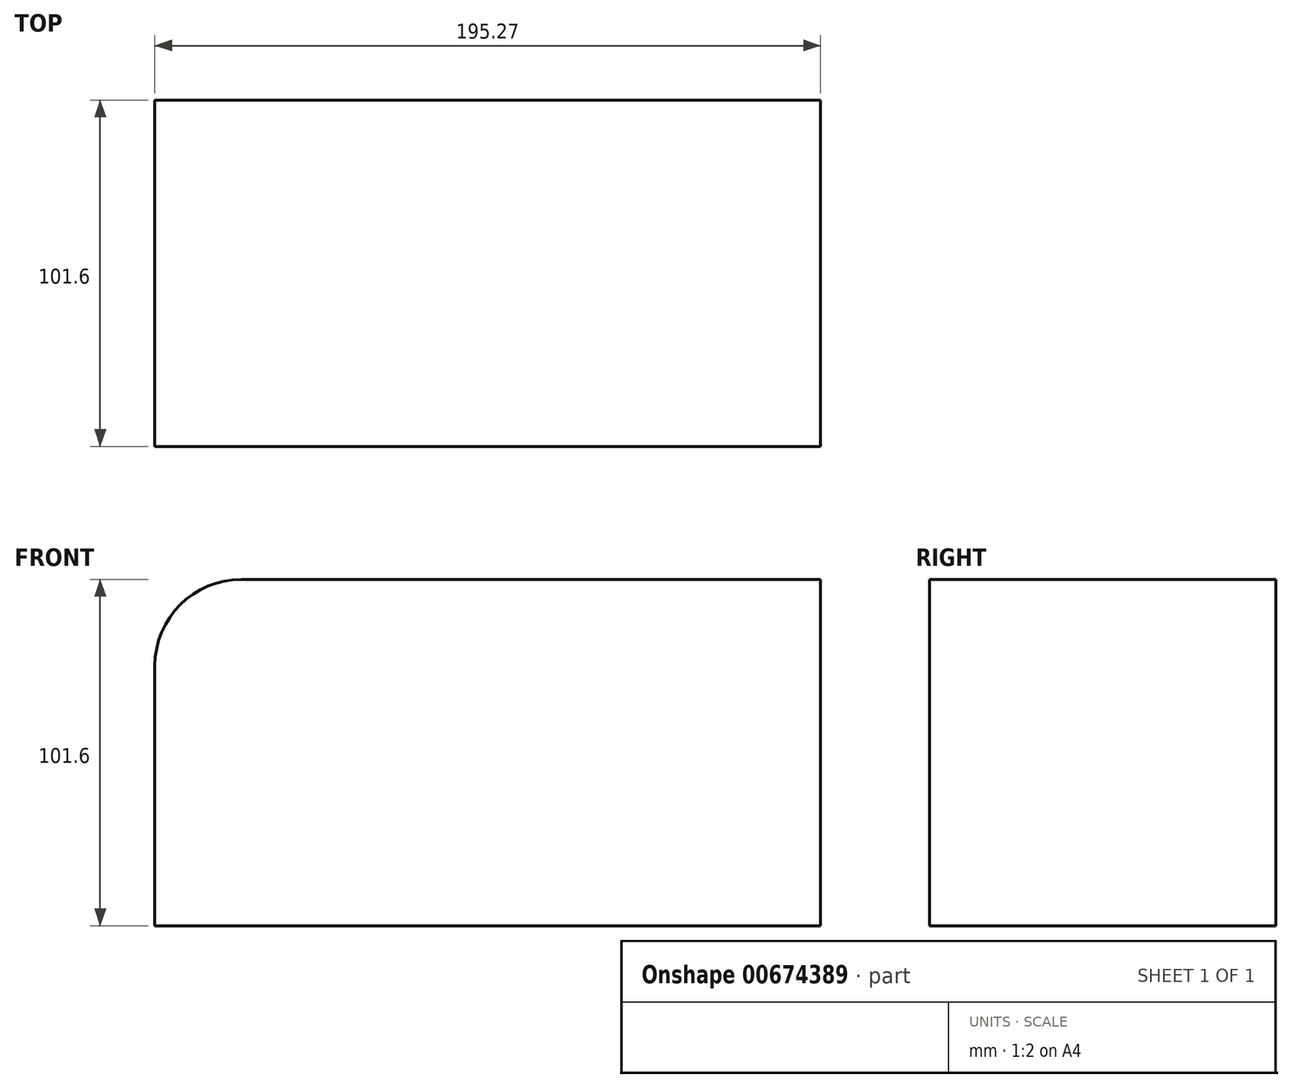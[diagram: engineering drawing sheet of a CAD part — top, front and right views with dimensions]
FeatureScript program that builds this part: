
annotation { "Feature Type Name" : "Feature", "Feature Type Description" : "" }
export const myFeature = defineFeature(function(context is Context, id is Id, definition is map)
    precondition{}
    {
        {
            var Q0;
            Q0=qCreatedBy(makeId("Front.planeOp"),FACE);
            var sketch = newSketch(context, id + "F0", { "sketchPlane" : qUnion([Q0])});
            skLineSegment(sketch, "E0.bottom", {"start": v(0, 0) * mm, "end": v(-195.27, 0) * mm});
            skLineSegment(sketch, "E0.top", {"start": v(0, 101.6) * mm, "end": v(-195.27, 101.6) * mm});
            skLineSegment(sketch, "E0.left", {"start": v(0, 0) * mm, "end": v(0, 101.6) * mm});
            skLineSegment(sketch, "E0.right", {"start": v(-195.27, 0) * mm, "end": v(-195.27, 101.6) * mm});
            skSolve(sketch);
        }
        {
            var Q0;
            Q0=makeQuery(id+"F0.imprint","IMPRINT",FACE,{"disambiguationData":[TD([[makeQuery(id+"F0.imprint","IMPRINT",EDGE,{"derivedFrom":sQuery(id+"F0.wireOp",EDGE,"E0.bottom")}),-1.0]])]});
            extrude(context, id + "F1", {"entities" : qUnion([Q0]), "depth" : 101.6 * mm, "offsetDistance" : 25.4 * mm});
        }
        {
            var Q0;
            Q0=makeQuery(id+"F1.opExtrude","SWEPT_FACE",FACE,{"disambiguationData":[OSD([sQuery(id+"F0.wireOp",EDGE,"E0.top")])]});
            var sketch = newSketch(context, id + "F2", { "sketchPlane" : qUnion([Q0])});
            skLineSegment(sketch, "E1.bottom", {"start": v(-124.53, 0) * mm, "end": v(-86.43, 0) * mm});
            skLineSegment(sketch, "E1.top", {"start": v(-124.53, -101.6) * mm, "end": v(-86.43, -101.6) * mm});
            skLineSegment(sketch, "E1.left", {"start": v(-124.53, 0) * mm, "end": v(-124.53, -101.6) * mm});
            skLineSegment(sketch, "E1.right", {"start": v(-86.43, 0) * mm, "end": v(-86.43, -101.6) * mm});
            skSolve(sketch);
        }
        {
            var Q0;
            Q0=makeQuery(id+"F2.imprint","IMPRINT",FACE,{"disambiguationData":[TD([[makeQuery(id+"F2.imprint","IMPRINT",EDGE,{"derivedFrom":sQuery(id+"F2.wireOp",EDGE,"E1.bottom")}),1.0]])]});
            extrude(context, id + "F3", {"entities" : qUnion([Q0]), "operationType" : NewBodyOperationType.ADD, "oppositeDirection" : true, "depth" : 76.2 * mm, "offsetDistance" : 25.4 * mm});
        }
        {
            var Q0;
            Q0=makeQuery(id+"F1.opExtrude","SWEPT_EDGE",EDGE,{"disambiguationData":[OSD([sQuery(id+"F0.wireOp",EDGE,"E0.top"),sQuery(id+"F0.wireOp",EDGE,"E0.right")])]});
            fillet(context, id + "F4", {"entities" : qUnion([Q0]), "radius" : 25.4 * mm, "tangentPropagation" : true, "allowEdgeOverflow" : false});
        }
    });
